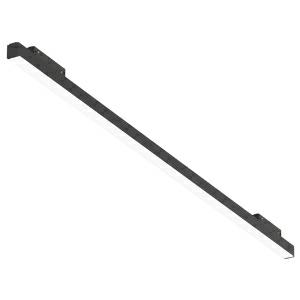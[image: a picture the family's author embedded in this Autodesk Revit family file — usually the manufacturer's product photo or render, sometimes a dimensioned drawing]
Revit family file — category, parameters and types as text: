
# Revit family: 2look4_25_magtrack_ledline_l_1020mm_led_48v_2700k_11w_cri80_810-0220_4b82
name_source: partatom
category: Leuchten
revit_build: Autodesk Revit 2016 (Build: 20190508_0715(x64)
units: mm (PartAtom-declared; Revit-internal decimal feet)

## family parameters
Basisbauteil = Fläche
Beim Laden mit Abzugskörper schneiden = Nein
Bemaßung runder Anschluss = Durchmesser verwenden
Gemeinsam genutzt = Nein
Lichtquelle = Nein
Raumberechnungspunkt = Nein
Teiletyp = Normal

## types (1)
- 810-0220 (10 x LED, 100 lm, 1.1 W, 2700K)
    Beschreibung = The insert consists of aluminum-die-cast. The ballast is integrated and allows for an operation with 48V. 2LOOK4 25 MAGTRACK / HYPRO 30 (# 810-0220) ist not dimmable (on/off).
    CIE Flux Codes = 56 84 97 99 60
    Color Rendering = 1A/90…99
    Color Temperature = 2700K
    Height = 0 mm  [stored 0 ft]
    Hersteller = Prolicht
    Lamp Light Flux = 100 lm
    Lamp Power = 1.1 W
    Lamp count = 10
    Lampe = 10 x LED
    Length = 1020 mm
    Luminous efficacy = 54 lm/W
    ModVariant = Nein
    Modell = 810-0220
    Mounting Place = Ceiling
    Mounting Type = Recessed
    Number of Poles = 1
    OnlyDefault = Ja
    Power Factor = 1
    Product Name = 2LOOK4 25 MAGTRACK__LEDLINE L=1020mm LED 48V 2700K 11W CRI80
    Product group = Trimless recessed profile systems
    ProductGroupID = 414
    Protection Class = Protection class
    Protection Degree = Degree of protection
    RLX_Detail_Level = 1
    RlxData = <blob elided: 298813 chars, md5=981060e8>
    Scheinlast = 11 VA
    Socket = socket
    Standby Power = 0 W
    System Light Flux = 597 lm
    System Power = 11 W
    Typenbild = 810-0220.jpg
    Typenkommentare = The insert consists of aluminum-die-cast. The ballast is integrated and allows for an operation with 48V. 2LOOK4 25 MAGTRACK / HYPRO 30 (# 810-0220) ist not dimmable (on/off).
    URL = http://relux.com
    VarID = 810-0220
    Voltage = 0 V
    Vorgabe-Ansicht = 1800 mm
    Weight = 0.00 kg
    Width = 23 mm

note: [stored X ft] marks values corroborated as IEEE doubles in the binary element streams (Revit-internal decimal feet)

## geometry (parser evidence)
native form markers: Blend x4, Sweep x13
no freeform markers — native parametric forms only
